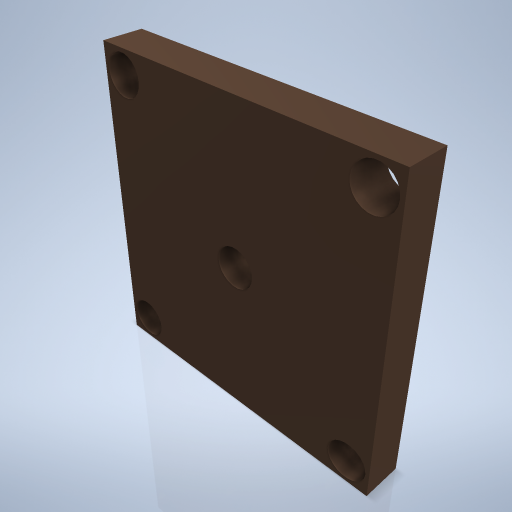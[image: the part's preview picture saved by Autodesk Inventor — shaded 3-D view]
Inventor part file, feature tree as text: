
AUTODESK INVENTOR PART (.ipt)
format: ipt  version: 2024.2 (Build 282272000, 272)  size: 239,616 bytes
history: native  units: mm
features: sketch x4, extrude x2, hole x2
ambient origin geometry x8: Origin, YZ Plane, XZ Plane, XY Plane, X Axis, Y Axis, Z Axis, Center Point
bodies: Volumenkörper1 (feature_tree)
feature tree (8):
  extrude  "Extrusion1"  Depth=50.0mm
  extrude  "Extrusion2"  Depth=6.5mm
  hole  "Bohrung1"  [1 undecoded]
  hole  "Bohrung2"  [1 undecoded]
  sketch  "Skizze1"  dims[d0=50.0mm d1=50.0mm]
  sketch  "Skizze2"  dims[d2=6.5mm d3=0.0mm d4=27.0mm]
  sketch  "Skizze3"  dims[d5=1.5mm d6=0.0mm]
  sketch  "Skizze4"  dims[d7=6.5mm d8=6.0mm d9=4.0mm d10=2.0mm d11=90.0deg d12=8.0mm d13=0.0mm d14=6.5mm d15=6.0mm d16=4.0mm d17=2.0mm d18=90.0deg d19=8.0mm d20=0.0mm d29=42.248mm]
note: 2 required parameter values undecoded (feature->parameter linkage not recoverable at this tier; creation-order binding heuristic only, values carry confidence <= 0.55)
